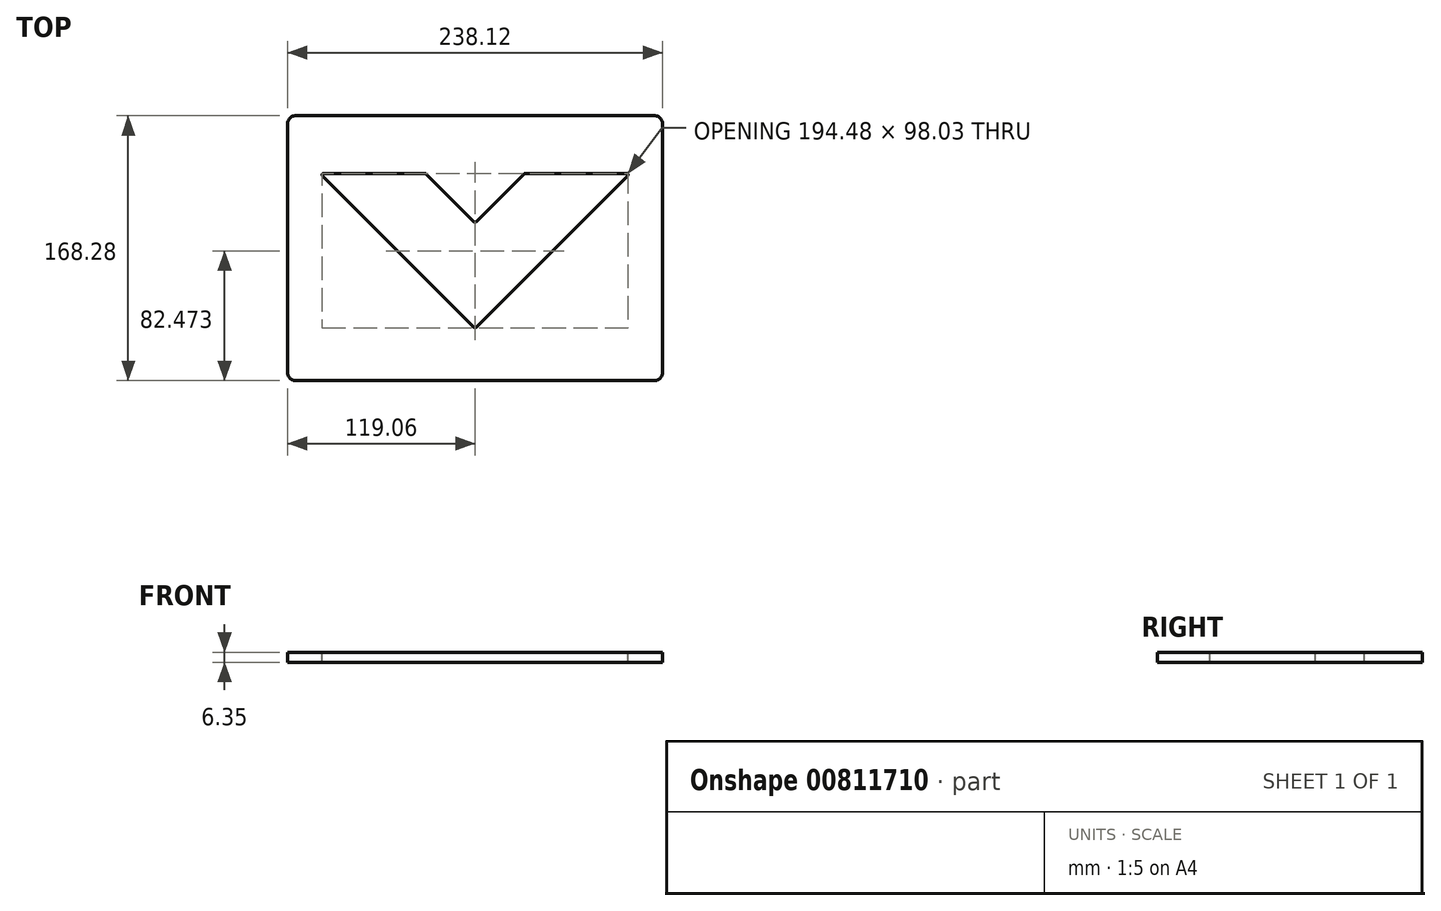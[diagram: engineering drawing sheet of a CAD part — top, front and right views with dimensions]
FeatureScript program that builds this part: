
annotation { "Feature Type Name" : "Feature", "Feature Type Description" : "" }
export const myFeature = defineFeature(function(context is Context, id is Id, definition is map)
    precondition{}
    {
        {
            var Q0;
            Q0=qCreatedBy(makeId("Top.planeOp"),FACE);
            var sketch = newSketch(context, id + "F0", { "sketchPlane" : qUnion([Q0])});
            skLineSegment(sketch, "E0.bottom", {"start": v(-113.98, 84.14) * mm, "end": v(113.98, 84.14) * mm});
            skLineSegment(sketch, "E0.top", {"start": v(-113.98, -84.14) * mm, "end": v(113.98, -84.14) * mm});
            skLineSegment(sketch, "E0.left", {"start": v(-119.06, 79.06) * mm, "end": v(-119.06, -79.06) * mm});
            skLineSegment(sketch, "E0.right", {"start": v(119.06, 79.06) * mm, "end": v(119.06, -79.06) * mm});
            skPoint(sketch, "E0.middle", {"position": v(0, 0) * mm});
            skPoint(sketch, "E1.visualSharp", {"position": v(-119.06, -84.14) * mm});
            skArc(sketch, "E1.filletArc", {"start": v(-119.06, -79.06) * mm, "mid": v(-117.57, -82.65) * mm, "end": v(-113.98, -84.14) * mm});
            skPoint(sketch, "E2.visualSharp", {"position": v(-119.06, 84.14) * mm});
            skArc(sketch, "E2.filletArc", {"start": v(-113.98, 84.14) * mm, "mid": v(-117.57, 82.65) * mm, "end": v(-119.06, 79.06) * mm});
            skPoint(sketch, "E3.visualSharp", {"position": v(119.06, 84.14) * mm});
            skArc(sketch, "E3.filletArc", {"start": v(119.06, 79.06) * mm, "mid": v(117.57, 82.65) * mm, "end": v(113.98, 84.14) * mm});
            skPoint(sketch, "E4.visualSharp", {"position": v(119.06, -84.14) * mm});
            skArc(sketch, "E4.filletArc", {"start": v(113.98, -84.14) * mm, "mid": v(117.57, -82.65) * mm, "end": v(119.06, -79.06) * mm});
            skSolve(sketch);
        }
        {
            var Q0;
            Q0 = qSketchRegion(id + "F0", true);
            extrude(context, id + "F1", {"entities" : qUnion([Q0]), "depth" : 6.35 * mm, "offsetDistance" : 25.4 * mm});
        }
        {
            var Q0;
            Q0=makeQuery(id+"F1.opExtrude","CAP_FACE",FACE,{"disambiguationData":[OSD([sQuery(id+"F0.wireOp",EDGE,"E0.bottom"),sQuery(id+"F0.wireOp",EDGE,"E0.top"),sQuery(id+"F0.wireOp",EDGE,"E0.left"),sQuery(id+"F0.wireOp",EDGE,"E0.right"),sQuery(id+"F0.wireOp",EDGE,"E1.filletArc"),sQuery(id+"F0.wireOp",EDGE,"E2.filletArc"),sQuery(id+"F0.wireOp",EDGE,"E3.filletArc"),sQuery(id+"F0.wireOp",EDGE,"E4.filletArc")])],"isStart":false});
            var sketch = newSketch(context, id + "F2", { "sketchPlane" : qUnion([Q0])});
            skLineSegment(sketch, "E5", {"start": v(0, -49.21) * mm, "end": v(-95.3, 46.08) * mm});
            skLineSegment(sketch, "E6", {"start": v(-95.3, 46.08) * mm, "end": v(-31.8, 46.08) * mm});
            skLineSegment(sketch, "E7", {"start": v(-31.8, 46.08) * mm, "end": v(0, 14.29) * mm});
            skLineSegment(sketch, "E8.MirrorCS", {"start": v(31.8, 46.08) * mm, "end": v(0, 14.29) * mm});
            skLineSegment(sketch, "E9.MirrorCS", {"start": v(95.3, 46.08) * mm, "end": v(31.8, 46.08) * mm});
            skLineSegment(sketch, "E10.MirrorCS", {"start": v(0, -49.21) * mm, "end": v(95.3, 46.08) * mm});
            skSolve(sketch);
        }
        {
            var Q0;
            Q0 = qSketchRegion(id + "F2", true);
            extrude(context, id + "F3", {"entities" : qUnion([Q0]), "operationType" : NewBodyOperationType.REMOVE, "endBound" : BoundingType.THROUGH_ALL, "oppositeDirection" : true, "depth" : 25.4 * mm, "offsetDistance" : 25.4 * mm});
        }
        {
            var Q0;
            Q0=makeQuery(id+"F1.opExtrude","CAP_FACE",FACE,{"disambiguationData":[OSD([sQuery(id+"F0.wireOp",EDGE,"E0.bottom"),sQuery(id+"F0.wireOp",EDGE,"E0.top"),sQuery(id+"F0.wireOp",EDGE,"E0.left"),sQuery(id+"F0.wireOp",EDGE,"E0.right"),sQuery(id+"F0.wireOp",EDGE,"E1.filletArc"),sQuery(id+"F0.wireOp",EDGE,"E2.filletArc"),sQuery(id+"F0.wireOp",EDGE,"E3.filletArc"),sQuery(id+"F0.wireOp",EDGE,"E4.filletArc")])],"isStart":false});
            var sketch = newSketch(context, id + "F4", { "sketchPlane" : qUnion([Q0])});
            skLineSegment(sketch, "E11.0", {"start": v(-0.56, -50.45) * mm, "end": v(-97.01, 46) * mm});
            skLineSegment(sketch, "E11.1", {"start": v(-31.03, 47.12) * mm, "end": v(-0.56, 16.64) * mm});
            skLineSegment(sketch, "E11.2", {"start": v(31.03, 47.12) * mm, "end": v(0.56, 16.64) * mm});
            skLineSegment(sketch, "E11.3", {"start": v(-96.46, 47.35) * mm, "end": v(-31.6, 47.35) * mm});
            skLineSegment(sketch, "E11.4", {"start": v(96.46, 47.35) * mm, "end": v(31.6, 47.35) * mm});
            skLineSegment(sketch, "E11.5", {"start": v(0.56, -50.45) * mm, "end": v(97.01, 46) * mm});
            skPoint(sketch, "E12.visualSharp", {"position": v(-31.26, 47.35) * mm});
            skArc(sketch, "E12.filletArc", {"start": v(-31.03, 47.12) * mm, "mid": v(-31.29, 47.29) * mm, "end": v(-31.6, 47.35) * mm});
            skPoint(sketch, "E13.visualSharp", {"position": v(0, 16.08) * mm});
            skArc(sketch, "E13.filletArc", {"start": v(-0.56, 16.64) * mm, "mid": v(0, 16.4) * mm, "end": v(0.56, 16.64) * mm});
            skPoint(sketch, "E14.visualSharp", {"position": v(31.26, 47.35) * mm});
            skArc(sketch, "E14.filletArc", {"start": v(31.6, 47.35) * mm, "mid": v(31.29, 47.29) * mm, "end": v(31.03, 47.12) * mm});
            skPoint(sketch, "E15.visualSharp", {"position": v(98.36, 47.35) * mm});
            skArc(sketch, "E15.filletArc", {"start": v(97.01, 46) * mm, "mid": v(97.18, 46.86) * mm, "end": v(96.46, 47.35) * mm});
            skPoint(sketch, "E16.visualSharp", {"position": v(0, -51) * mm});
            skArc(sketch, "E16.filletArc", {"start": v(-0.56, -50.45) * mm, "mid": v(0, -50.68) * mm, "end": v(0.56, -50.45) * mm});
            skPoint(sketch, "E17.visualSharp", {"position": v(-98.36, 47.35) * mm});
            skArc(sketch, "E17.filletArc", {"start": v(-96.46, 47.35) * mm, "mid": v(-97.18, 46.86) * mm, "end": v(-97.01, 46) * mm});
            skSolve(sketch);
        }
        {
            var Q0;
            Q0 = qSketchRegion(id + "F4", true);
            extrude(context, id + "F5", {"entities" : qUnion([Q0]), "operationType" : NewBodyOperationType.REMOVE, "endBound" : BoundingType.THROUGH_ALL, "oppositeDirection" : true, "depth" : 25.4 * mm, "offsetDistance" : 25.4 * mm});
        }
    });
